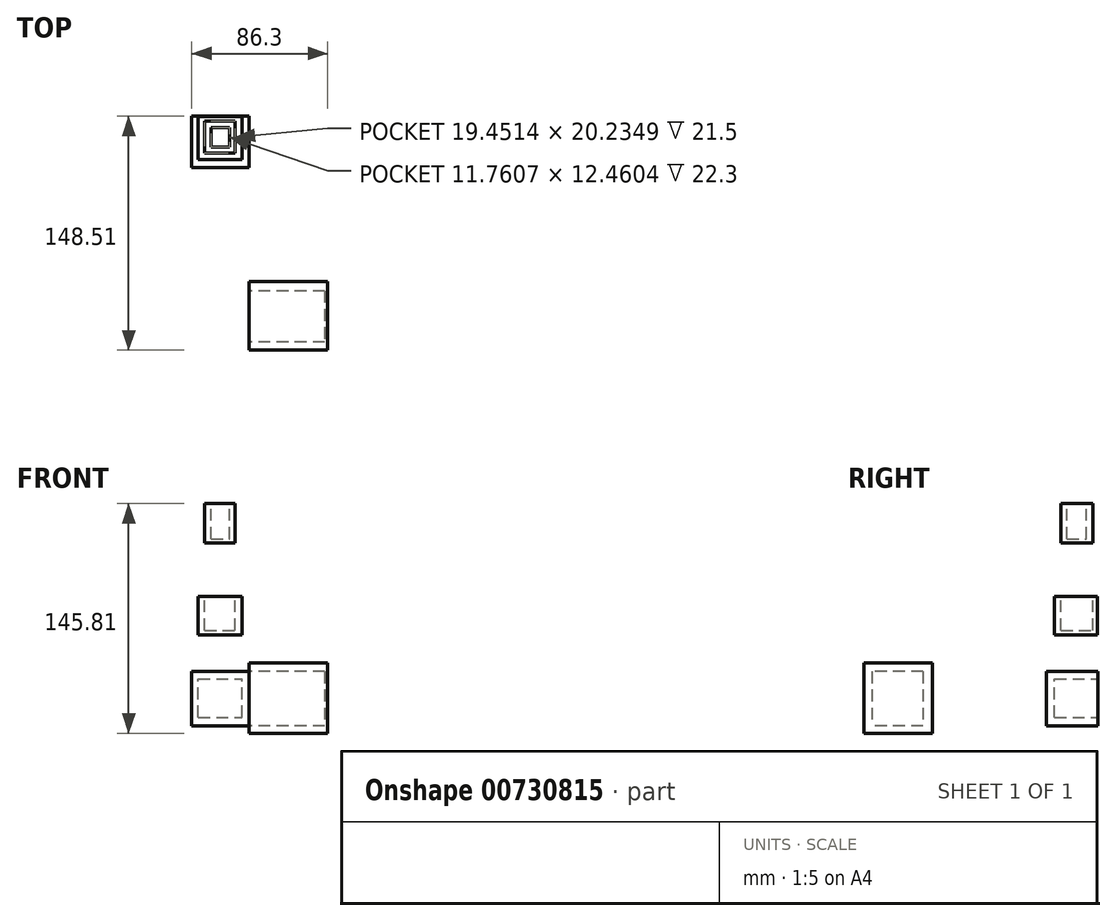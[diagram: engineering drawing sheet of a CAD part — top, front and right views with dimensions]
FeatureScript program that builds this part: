
annotation { "Feature Type Name" : "Feature", "Feature Type Description" : "" }
export const myFeature = defineFeature(function(context is Context, id is Id, definition is map)
    precondition{}
    {
        {
            var Q0;
            Q0=qCreatedBy(makeId("Top.planeOp"),FACE);
            var sketch = newSketch(context, id + "F0", { "sketchPlane" : qUnion([Q0])});
            skLineSegment(sketch, "E0.bottom", {"start": v(-34.98, 21.94) * mm, "end": v(15.02, 21.94) * mm});
            skLineSegment(sketch, "E0.top", {"start": v(-34.98, -21.54) * mm, "end": v(15.02, -21.54) * mm});
            skLineSegment(sketch, "E0.left", {"start": v(-34.98, 21.94) * mm, "end": v(-34.98, -21.54) * mm});
            skLineSegment(sketch, "E0.right", {"start": v(15.02, 21.94) * mm, "end": v(15.02, -21.54) * mm});
            skSolve(sketch);
        }
        {
            var Q0;
            Q0=makeQuery(id+"F0.imprint","IMPRINT",FACE,{"disambiguationData":[TD([[makeQuery(id+"F0.imprint","IMPRINT",EDGE,{"derivedFrom":sQuery(id+"F0.wireOp",EDGE,"E0.bottom")}),-1.0]])]});
            extrude(context, id + "F1", {"entities" : qUnion([Q0]), "depth" : 44.7 * mm, "offsetDistance" : 25 * mm});
        }
        {
            var Q0;
            Q0=makeQuery(id+"F1.opExtrude","SWEPT_FACE",FACE,{"disambiguationData":[OSD([sQuery(id+"F0.wireOp",EDGE,"E0.left")])]});
            var sketch = newSketch(context, id + "F2", { "sketchPlane" : qUnion([Q0])});
            skLineSegment(sketch, "E1.bottom", {"start": v(-16.07, 39.2) * mm, "end": v(16.38, 39.2) * mm});
            skLineSegment(sketch, "E1.top", {"start": v(-16.07, 4.73) * mm, "end": v(16.38, 4.73) * mm});
            skLineSegment(sketch, "E1.left", {"start": v(-16.07, 39.2) * mm, "end": v(-16.07, 4.73) * mm});
            skLineSegment(sketch, "E1.right", {"start": v(16.38, 39.2) * mm, "end": v(16.38, 4.73) * mm});
            skSolve(sketch);
        }
        {
            var Q0;
            Q0 = qSketchRegion(id + "F2", true);
            extrude(context, id + "F3", {"entities" : qUnion([Q0]), "operationType" : NewBodyOperationType.REMOVE, "oppositeDirection" : true, "depth" : 48.1 * mm, "offsetDistance" : 25 * mm});
        }
        {
            var Q0;
            Q0=makeQuery(id+"F2.imprint","IMPRINT",FACE,{"disambiguationData":[TD([[makeQuery(id+"F2.imprint","IMPRINT",EDGE,{"derivedFrom":sQuery(id+"F2.wireOp",EDGE,"E1.bottom")}),-1.0]])]});
            extrude(context, id + "F4", {"entities" : qUnion([Q0]), "depth" : 36.3 * mm, "offsetDistance" : 25 * mm});
        }
        {
            var Q0;
            Q0=makeQuery(id+"F4.opExtrude","SWEPT_BODY",BODY,{"disambiguationData":[OSD([sQuery(id+"F2.wireOp",EDGE,"E1.bottom"),sQuery(id+"F2.wireOp",EDGE,"E1.top"),sQuery(id+"F2.wireOp",EDGE,"E1.left"),sQuery(id+"F2.wireOp",EDGE,"E1.right")])]});
            transform(context, id + "F5", {"entities" : qUnion([Q0]), "transformType" : TransformType.TRANSLATION_3D, "dx" : 0 * mm, "dy" : 110.9 * mm, "dz" : 0 * mm, "makeCopy" : false});
        }
        {
            var Q0;
            Q0=makeQuery(id+"F4.opExtrude","SWEPT_FACE",FACE,{"disambiguationData":[OSD([sQuery(id+"F2.wireOp",EDGE,"E1.left")])]});
            var sketch = newSketch(context, id + "F6", { "sketchPlane" : qUnion([Q0])});
            skLineSegment(sketch, "E2.bottom", {"start": v(67.12, 10.03) * mm, "end": v(39.26, 10.03) * mm});
            skLineSegment(sketch, "E2.top", {"start": v(67.12, 34.6) * mm, "end": v(39.26, 34.6) * mm});
            skLineSegment(sketch, "E2.left", {"start": v(67.12, 10.03) * mm, "end": v(67.12, 34.6) * mm});
            skLineSegment(sketch, "E2.right", {"start": v(39.26, 10.03) * mm, "end": v(39.26, 34.6) * mm});
            skSolve(sketch);
        }
        {
            var Q0;
            Q0 = qSketchRegion(id + "F6", true);
            extrude(context, id + "F7", {"entities" : qUnion([Q0]), "operationType" : NewBodyOperationType.REMOVE, "oppositeDirection" : true, "depth" : 27.4 * mm, "offsetDistance" : 25 * mm});
        }
        {
            var Q0;
            Q0=makeQuery(id+"F7.boolean.opBoolean","COPY",FACE,{"derivedFrom":makeQuery(id+"F7.opExtrude","CAP_FACE",FACE,{"disambiguationData":[OSD([sQuery(id+"F6.wireOp",EDGE,"E2.bottom"),sQuery(id+"F6.wireOp",EDGE,"E2.top"),sQuery(id+"F6.wireOp",EDGE,"E2.left"),sQuery(id+"F6.wireOp",EDGE,"E2.right")])],"isStart":false})});
            extrude(context, id + "F8", {"entities" : qUnion([Q0]), "depth" : 27.1 * mm, "offsetDistance" : 25 * mm});
        }
        {
            var Q0;
            Q0=makeQuery(id+"F8.opExtrude","SWEPT_BODY",BODY,{"disambiguationData":[OSD([sQuery(id+"F6.wireOp",EDGE,"E2.bottom"),sQuery(id+"F6.wireOp",EDGE,"E2.top"),sQuery(id+"F6.wireOp",EDGE,"E2.left"),sQuery(id+"F6.wireOp",EDGE,"E2.right")])]});
            transform(context, id + "F9", {"entities" : qUnion([Q0]), "transformType" : TransformType.TRANSLATION_3D, "dx" : 0 * mm, "dy" : 0 * mm, "dz" : 52.3 * mm, "makeCopy" : false});
        }
        {
            var Q0;
            Q0=makeQuery(id+"F8.opExtrude","SWEPT_FACE",FACE,{"disambiguationData":[OSD([sQuery(id+"F6.wireOp",EDGE,"E2.top")])]});
            var sketch = newSketch(context, id + "F10", { "sketchPlane" : qUnion([Q0])});
            skLineSegment(sketch, "E3.bottom", {"start": v(-63.07, 103.63) * mm, "end": v(-43.62, 103.63) * mm});
            skLineSegment(sketch, "E3.top", {"start": v(-63.07, 123.87) * mm, "end": v(-43.62, 123.87) * mm});
            skLineSegment(sketch, "E3.left", {"start": v(-63.07, 103.63) * mm, "end": v(-63.07, 123.87) * mm});
            skLineSegment(sketch, "E3.right", {"start": v(-43.62, 103.63) * mm, "end": v(-43.62, 123.87) * mm});
            skSolve(sketch);
        }
        {
            var Q0;
            Q0=makeQuery(id+"F10.imprint","IMPRINT",FACE,{"disambiguationData":[TD([[makeQuery(id+"F10.imprint","IMPRINT",EDGE,{"derivedFrom":sQuery(id+"F10.wireOp",EDGE,"E3.bottom")}),1.0]])]});
            extrude(context, id + "F11", {"entities" : qUnion([Q0]), "operationType" : NewBodyOperationType.REMOVE, "oppositeDirection" : true, "depth" : 21.5 * mm, "offsetDistance" : 25 * mm});
        }
        {
            var Q0;
            Q0=makeQuery(id+"F10.imprint","IMPRINT",FACE,{"disambiguationData":[TD([[makeQuery(id+"F10.imprint","IMPRINT",EDGE,{"derivedFrom":sQuery(id+"F10.wireOp",EDGE,"E3.bottom")}),1.0]])]});
            extrude(context, id + "F12", {"entities" : qUnion([Q0]), "depth" : 25 * mm, "offsetDistance" : 25 * mm});
        }
        {
            var Q0;
            Q0=makeQuery(id+"F12.opExtrude","SWEPT_BODY",BODY,{"disambiguationData":[OSD([sQuery(id+"F10.wireOp",EDGE,"E3.bottom"),sQuery(id+"F10.wireOp",EDGE,"E3.top"),sQuery(id+"F10.wireOp",EDGE,"E3.left"),sQuery(id+"F10.wireOp",EDGE,"E3.right")])]});
            transform(context, id + "F13", {"entities" : qUnion([Q0]), "transformType" : TransformType.TRANSLATION_3D, "dx" : 0 * mm, "dy" : 0 * mm, "dz" : 33.9 * mm, "makeCopy" : false});
        }
        {
            var Q0;
            Q0=makeQuery(id+"F12.opExtrude","CAP_FACE",FACE,{"disambiguationData":[OSD([sQuery(id+"F10.wireOp",EDGE,"E3.bottom"),sQuery(id+"F10.wireOp",EDGE,"E3.top"),sQuery(id+"F10.wireOp",EDGE,"E3.left"),sQuery(id+"F10.wireOp",EDGE,"E3.right")])],"isStart":false});
            var sketch = newSketch(context, id + "F14", { "sketchPlane" : qUnion([Q0])});
            skLineSegment(sketch, "E4.bottom", {"start": v(-58.93, 107.46) * mm, "end": v(-47.17, 107.46) * mm});
            skLineSegment(sketch, "E4.top", {"start": v(-58.93, 119.92) * mm, "end": v(-47.17, 119.92) * mm});
            skLineSegment(sketch, "E4.left", {"start": v(-58.93, 107.46) * mm, "end": v(-58.93, 119.92) * mm});
            skLineSegment(sketch, "E4.right", {"start": v(-47.17, 107.46) * mm, "end": v(-47.17, 119.92) * mm});
            skSolve(sketch);
        }
        {
            var Q0;
            Q0=makeQuery(id+"F14.imprint","IMPRINT",FACE,{"disambiguationData":[TD([[makeQuery(id+"F14.imprint","IMPRINT",EDGE,{"derivedFrom":sQuery(id+"F14.wireOp",EDGE,"E4.bottom")}),1.0]])]});
            extrude(context, id + "F15", {"entities" : qUnion([Q0]), "operationType" : NewBodyOperationType.REMOVE, "oppositeDirection" : true, "depth" : 22.3 * mm, "offsetDistance" : 25 * mm});
        }
    });
